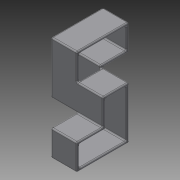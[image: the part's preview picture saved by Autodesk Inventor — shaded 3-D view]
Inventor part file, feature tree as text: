
AUTODESK INVENTOR PART (.ipt)
format: ipt  version: 2014 (Build 180170000, 170)  size: 243,712 bytes
history: native  units: in
note: dims shown in document units (in); Inventor stores cm internally (conversion verified against a paired STEP export)
features: plane x8, extrude x3, other x1, shell x1, fillet x1, sketch x1
ambient origin geometry x8: Origin, YZ Plane, XZ Plane, XY Plane, X Axis, Y Axis, Z Axis, Center Point
bodies: Solid1 (feature_tree)
feature tree (15):
  other  "Cube Master.ipt"
  extrude  "Extrusion1"  Depth=0.3937in
  extrude  "Extrusion2"  Depth=0.0193in TaperAngle=0.0deg
  extrude  "Extrusion3"  Depth=0.0193in TaperAngle=0.0deg
  shell  "Shell1"  Thickness=1.0in
  fillet  "Fillet1"  Radius=0.0394in
  sketch  "Sketch1"  dims[d0=0.3937in d1=0.3937in d2=1.0in d3=0.0in d4=1.0in d5=0.0in d6=1.0in d7=0.0in d8=0.0394in d9=0.0193in d10=0.0193in]
  plane  "Work Plane1"
  plane  "Work Plane2"
  plane  "Work Plane3"
  plane  "Work Plane4"
  plane  "Work Plane5"
  plane  "Work Plane6"
  plane  "Work Plane7"
  plane  "Work Plane8"
